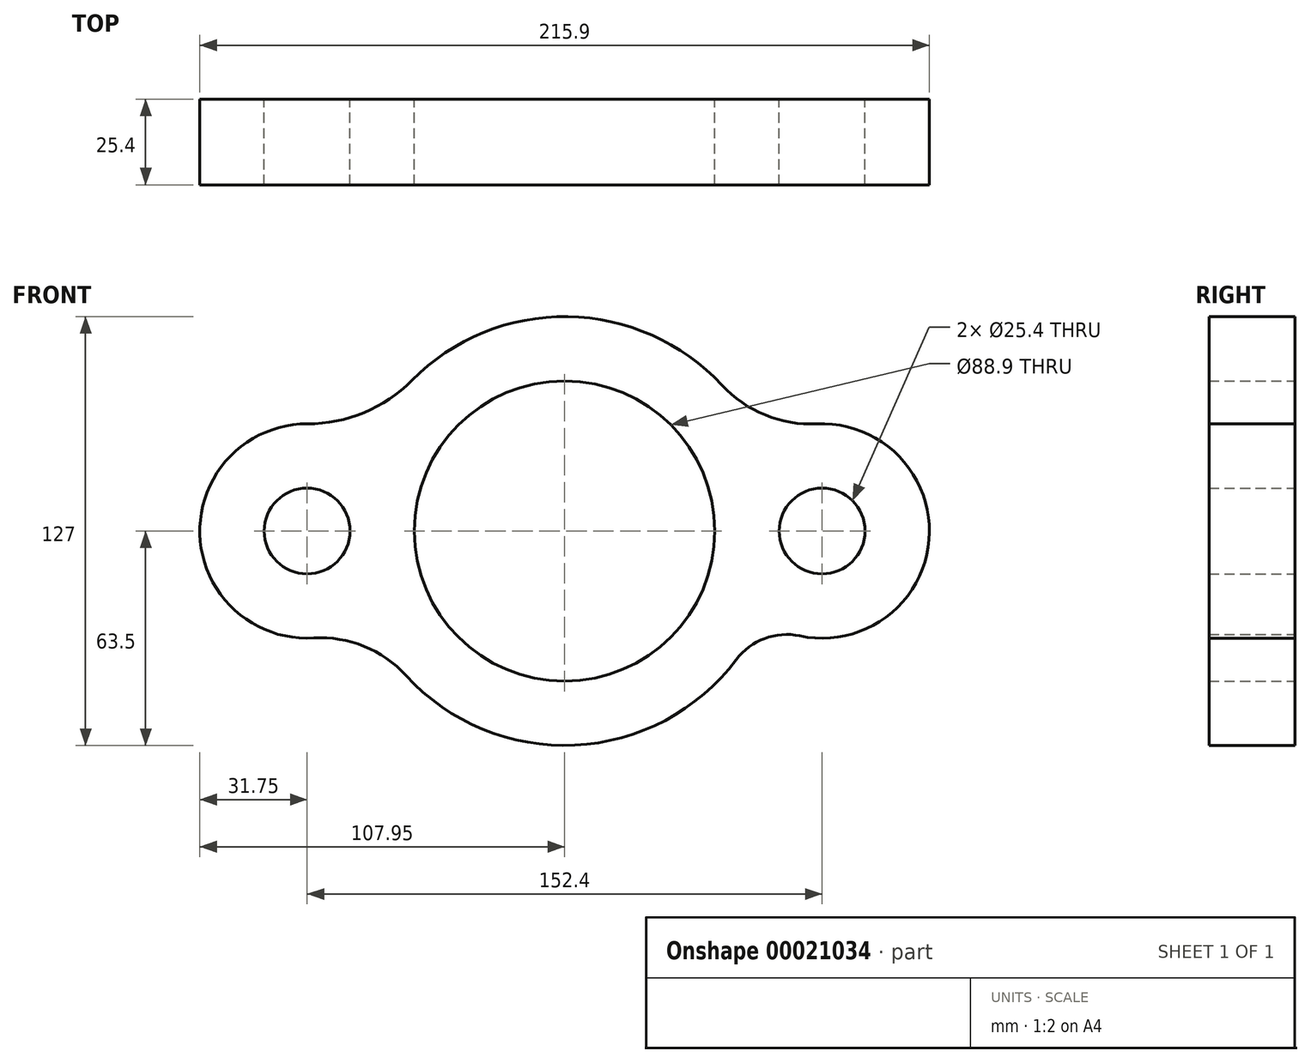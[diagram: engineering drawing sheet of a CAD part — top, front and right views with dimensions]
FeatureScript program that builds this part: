
annotation { "Feature Type Name" : "Feature", "Feature Type Description" : "" }
export const myFeature = defineFeature(function(context is Context, id is Id, definition is map)
    precondition{}
    {
        {
            var Q0;
            Q0=qCreatedBy(makeId("Front.planeOp"),FACE);
            var sketch = newSketch(context, id + "F0", { "sketchPlane" : qUnion([Q0])});
            skCircle(sketch, "E0", {"center": v(0, 0) * mm, "radius": 44.45 * mm});
            skCircle(sketch, "E1", {"center": v(-76.2, 0) * mm, "radius": 12.7 * mm});
            skCircle(sketch, "E2", {"center": v(76.2, 0) * mm, "radius": 12.7 * mm});
            skArc(sketch, "E3", {"start": v(-46.94, -42.77) * mm, "mid": v(3.04, -63.43) * mm, "end": v(50.8, -38.09) * mm});
            skArc(sketch, "E4", {"start": v(-76.1, 31.75) * mm, "mid": v(-107.94, -0.92) * mm, "end": v(-74.26, -31.7) * mm});
            skArc(sketch, "E5", {"start": v(69.58, -31.05) * mm, "mid": v(107.85, -2.58) * mm, "end": v(74.7, 31.71) * mm});
            skArc(sketch, "E6", {"start": v(-76.1, 31.75) * mm, "mid": v(-59.35, 35.07) * mm, "end": v(-45.2, 44.6) * mm});
            skArc(sketch, "E7", {"start": v(46.54, 43.2) * mm, "mid": v(59.34, 34.35) * mm, "end": v(74.7, 31.71) * mm});
            skArc(sketch, "E8", {"start": v(-46.94, -42.77) * mm, "mid": v(-59.34, -34.13) * mm, "end": v(-74.26, -31.7) * mm});
            skArc(sketch, "E9", {"start": v(69.58, -31.05) * mm, "mid": v(59.16, -31.83) * mm, "end": v(50.8, -38.09) * mm});
            skArc(sketch, "E10.trimOffspring", {"start": v(46.54, 43.2) * mm, "mid": v(0.97, 63.5) * mm, "end": v(-45.2, 44.6) * mm});
            skSolve(sketch);
        }
        {
            var Q0;
            Q0 = qSketchRegion(id + "F0", true);
            extrude(context, id + "F1", {"entities" : qUnion([Q0]), "depth" : 25.4 * mm});
        }
    });
